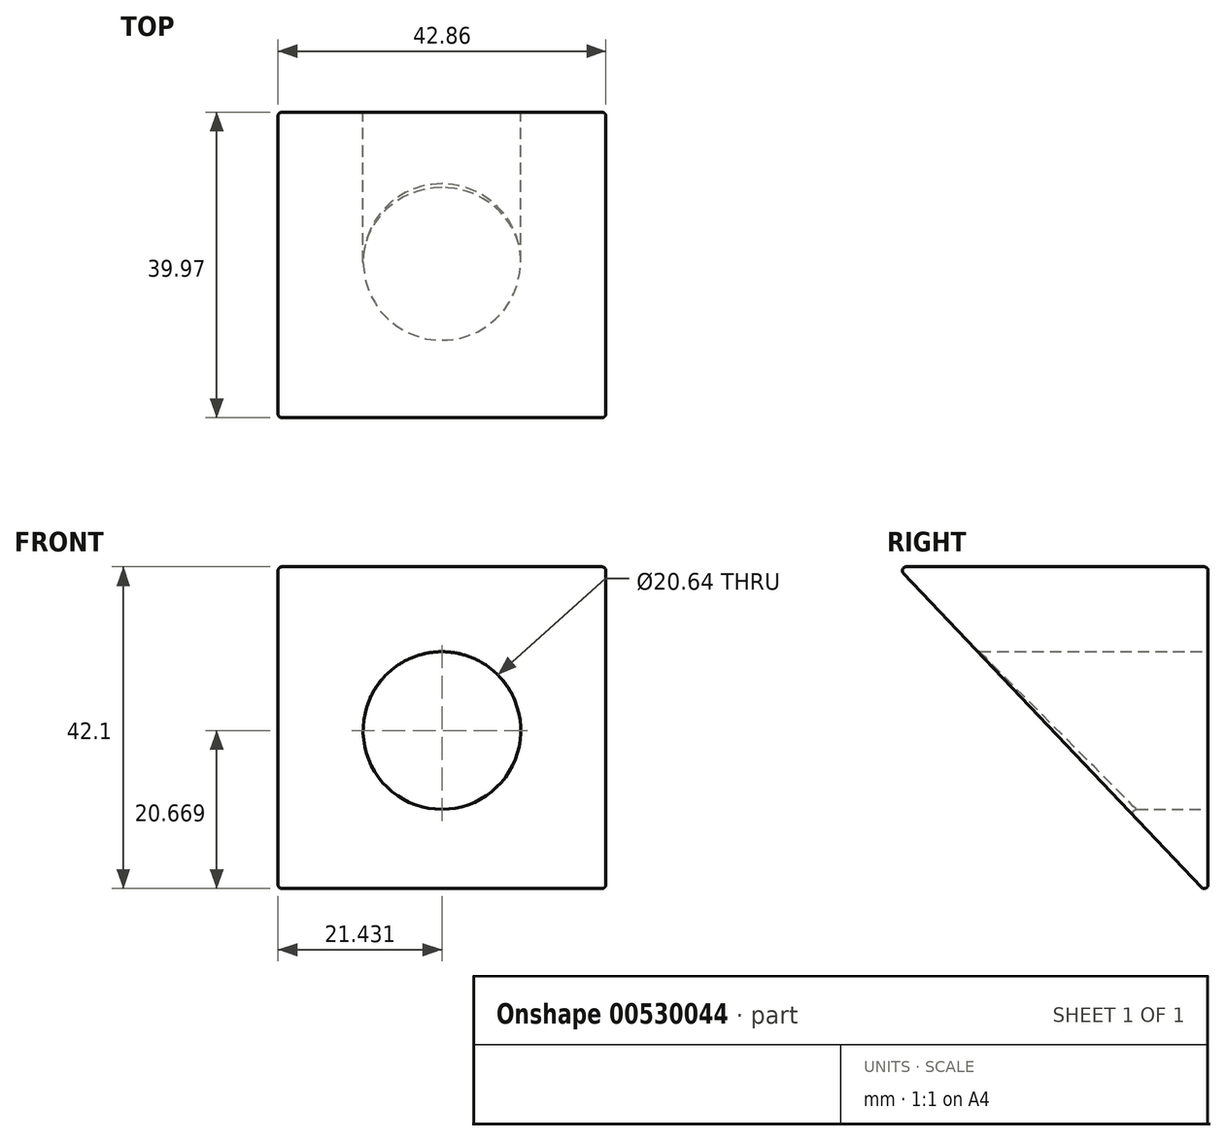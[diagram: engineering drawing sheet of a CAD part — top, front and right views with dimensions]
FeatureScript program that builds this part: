
annotation { "Feature Type Name" : "Feature", "Feature Type Description" : "" }
export const myFeature = defineFeature(function(context is Context, id is Id, definition is map)
    precondition{}
    {
        {
            var Q0;
            Q0=qCreatedBy(makeId("Front.planeOp"),FACE);
            var sketch = newSketch(context, id + "F0", { "sketchPlane" : qUnion([Q0])});
            skLineSegment(sketch, "E0.bottom", {"start": v(0, 0) * mm, "end": v(42.86, 0) * mm});
            skLineSegment(sketch, "E0.top", {"start": v(0, -42.86) * mm, "end": v(42.86, -42.86) * mm});
            skLineSegment(sketch, "E0.left", {"start": v(0, 0) * mm, "end": v(0, -42.86) * mm});
            skLineSegment(sketch, "E0.right", {"start": v(42.86, 0) * mm, "end": v(42.86, -42.86) * mm});
            skLineSegment(sketch, "E1", {"start": v(21.43, 0) * mm, "end": v(21.43, -42.86) * mm, "construction": true});
            skCircle(sketch, "E2", {"center": v(21.43, -21.43) * mm, "radius": 10.32 * mm});
            skSolve(sketch);
        }
        {
            var Q0;
            Q0=qSketchRegion(id+"F0",true);
            extrude(context, id + "F1", {"entities" : qUnion([Q0]), "depth" : 40.64 * mm});
        }
        {
            var Q0;
            Q0=makeQuery(id+"F1.opExtrude","SWEPT_FACE",FACE,{"disambiguationData":[OSD([sQuery(id+"F0.wireOp",EDGE,"E0.right")])]});
            var sketch = newSketch(context, id + "F2", { "sketchPlane" : qUnion([Q0])});
            skLineSegment(sketch, "E3", {"start": v(-40.64, 0) * mm, "end": v(0, -42.86) * mm});
            skLineSegment(sketch, "E4", {"start": v(-40.64, 0) * mm, "end": v(-40.64, -42.86) * mm});
            skLineSegment(sketch, "E5", {"start": v(-40.64, -42.86) * mm, "end": v(0, -42.86) * mm});
            skSolve(sketch);
        }
        {
            var Q0;
            Q0=qSketchRegion(id+"F2",true);
            extrude(context, id + "F3", {"entities" : qUnion([Q0]), "operationType" : NewBodyOperationType.REMOVE, "endBound" : BoundingType.THROUGH_ALL, "oppositeDirection" : true, "depth" : 25.4 * mm});
        }
        {
            var Q0;
            Q0=makeQuery(id+"F1.opExtrude","SWEPT_FACE",FACE,{"disambiguationData":[OSD([sQuery(id+"F0.wireOp",EDGE,"E0.right")])]});
            var Q1;
            Q1=makeQuery(id+"F3.boolean.opBoolean","COPY",FACE,{"derivedFrom":makeQuery(id+"F3.opExtrude","SWEPT_FACE",FACE,{"disambiguationData":[OSD([sQuery(id+"F2.wireOp",EDGE,"E3")])]})});
            var Q2;
            Q2=makeQuery(id+"F1.opExtrude","SWEPT_FACE",FACE,{"disambiguationData":[OSD([sQuery(id+"F0.wireOp",EDGE,"E0.left")])]});
            var Q3;
            Q3=makeQuery(id+"F1.opExtrude","CAP_EDGE",EDGE,{"disambiguationData":[OSD([sQuery(id+"F0.wireOp",EDGE,"E0.bottom")])],"isStart":true});
            fillet(context, id + "F4", {"entities" : qUnion([Q0, Q1, Q2, Q3]), "radius" : 0.5 * mm, "tangentPropagation" : true, "allowEdgeOverflow" : false});
        }
    });
